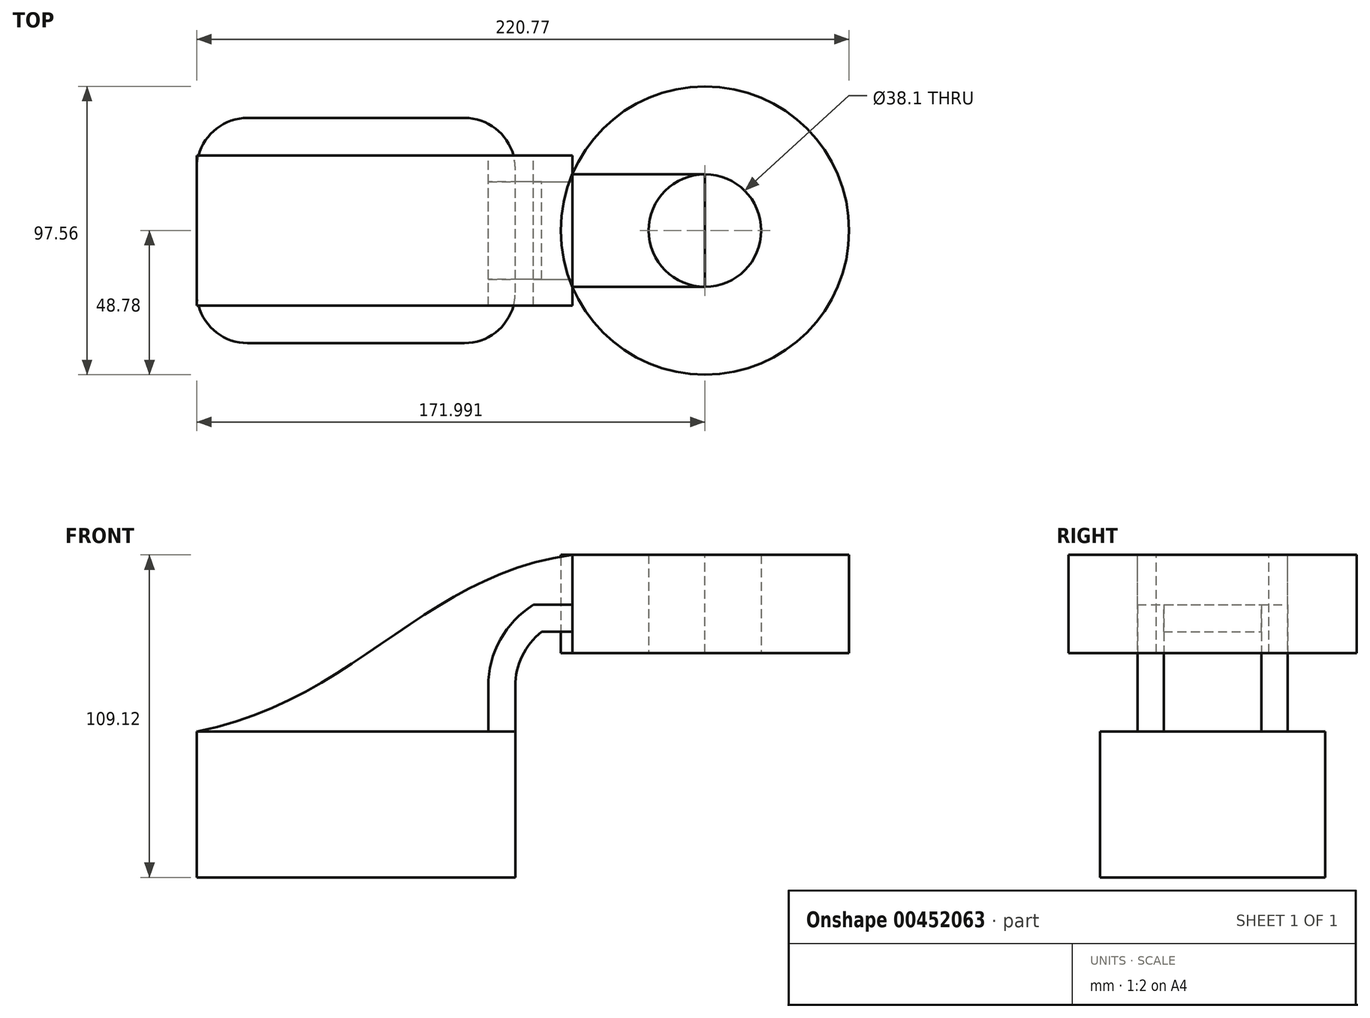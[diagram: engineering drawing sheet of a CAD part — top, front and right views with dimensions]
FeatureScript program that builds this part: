
annotation { "Feature Type Name" : "Feature", "Feature Type Description" : "" }
export const myFeature = defineFeature(function(context is Context, id is Id, definition is map)
    precondition{}
    {
        {
            var Q0;
            Q0=qCreatedBy(makeId("Front.planeOp"),FACE);
            var sketch = newSketch(context, id + "F0", { "sketchPlane" : qUnion([Q0])});
            skLineSegment(sketch, "E0.bottom", {"start": v(-53.89, 24.7) * mm, "end": v(53.89, 24.7) * mm});
            skLineSegment(sketch, "E0.top", {"start": v(-53.89, -24.7) * mm, "end": v(53.89, -24.7) * mm});
            skLineSegment(sketch, "E0.left", {"start": v(-53.89, 24.7) * mm, "end": v(-53.89, -24.7) * mm});
            skLineSegment(sketch, "E0.right", {"start": v(53.89, 24.7) * mm, "end": v(53.89, -24.7) * mm});
            skPoint(sketch, "E0.middle", {"position": v(0, 0) * mm});
            skLineSegment(sketch, "E1.bottom", {"start": v(118.1, 51.2) * mm, "end": v(73.2, 51.2) * mm});
            skLineSegment(sketch, "E1.top", {"start": v(118.1, 84.42) * mm, "end": v(73.2, 84.42) * mm});
            skLineSegment(sketch, "E1.left", {"start": v(118.1, 51.2) * mm, "end": v(118.1, 84.42) * mm});
            skLineSegment(sketch, "E1.right", {"start": v(73.2, 51.2) * mm, "end": v(73.2, 84.42) * mm});
            skPoint(sketch, "E1.middle", {"position": v(95.65, 67.8) * mm});
            skLineSegment(sketch, "E2", {"start": v(53.89, 24.7) * mm, "end": v(53.89, 39.97) * mm});
            skArc(sketch, "E3", {"start": v(62.87, 58.38) * mm, "mid": v(56.25, 50.2) * mm, "end": v(53.89, 39.97) * mm});
            skLineSegment(sketch, "E4", {"start": v(62.87, 58.38) * mm, "end": v(95.65, 58.38) * mm});
            skLineSegment(sketch, "E5.0", {"start": v(60, 67.52) * mm, "end": v(95.65, 67.52) * mm});
            skArc(sketch, "E5.1", {"start": v(60, 67.52) * mm, "mid": v(48.81, 55.72) * mm, "end": v(44.74, 39.97) * mm});
            skLineSegment(sketch, "E5.2", {"start": v(44.74, 24.7) * mm, "end": v(44.74, 39.97) * mm});
            skFitSpline(sketch, "E6", {"points": [v(-53.89, 24.7) * mm, v(73.2, 84.42) * mm], "startDerivative": vector(161.66, 30.98) * mm, "endDerivative": vector(152.23, 20.2) * mm});
            skSolve(sketch);
        }
        {
            var Q0;
            Q0=makeQuery(id+"F0.imprint","IMPRINT",FACE,{"disambiguationData":[TD([[makeQuery(id+"F0.imprint","IMPRINT",EDGE,{"derivedFrom":sQuery(id+"F0.wireOp",EDGE,"E0.top")}),1.0]])]});
            extrude(context, id + "F1", {"entities" : qUnion([Q0]), "endBound" : BoundingType.SYMMETRIC, "depth" : 76.2 * mm});
        }
        {
            var Q0;
            {var subQ1=sQuery(id+"F0.wireOp",EDGE,"E1.bottom");Q0=makeQuery(id+"F0.imprint","IMPRINT",FACE,{"disambiguationData":[TD([[makeQuery(id+"F0.imprint","IMPRINT",EDGE,{"derivedFrom":subQ1}),-1.0]])]});}
            extrude(context, id + "F2", {"entities" : qUnion([Q0]), "endBound" : BoundingType.SYMMETRIC, "depth" : 38.1 * mm});
        }
        {
            var Q0;
            {var subQ0=sQuery(id+"F0.wireOp",EDGE,"E5.1");Q0=makeQuery(id+"F0.imprint","IMPRINT",FACE,{"disambiguationData":[TD([[makeQuery(id+"F0.imprint","IMPRINT",EDGE,{"derivedFrom":subQ0}),-1.0]])]});}
            extrude(context, id + "F3", {"entities" : qUnion([Q0]), "endBound" : BoundingType.SYMMETRIC, "depth" : 50.8 * mm});
        }
        {
            var Q0;
            {var subQ1=sQuery(id+"F0.wireOp",EDGE,"E2");Q0=makeQuery(id+"F0.imprint","IMPRINT",FACE,{"disambiguationData":[TD([[makeQuery(id+"F0.imprint","IMPRINT",EDGE,{"derivedFrom":subQ1}),1.0]])]});}
            extrude(context, id + "F4", {"entities" : qUnion([Q0]), "endBound" : BoundingType.SYMMETRIC, "depth" : 33.02 * mm});
        }
        {
            var Q0;
            Q0=makeQuery(id+"F2.opExtrude","CAP_FACE",FACE,{"disambiguationData":[OSD([sQuery(id+"F0.wireOp",EDGE,"E1.bottom"),sQuery(id+"F0.wireOp",EDGE,"E1.top"),sQuery(id+"F0.wireOp",EDGE,"E1.left"),sQuery(id+"F0.wireOp",EDGE,"E1.right")])],"isStart":false});
            var Q1;
            Q1=sQuery(id+"F0.wireOp",EDGE,"E1.left");
            revolve(context, id + "F5", {"entities" : qUnion([Q0]), "axis" : qUnion([Q1]), "revolveType" : RevolveType.FULL});
        }
        {
            var Q0;
            Q0=makeQuery(id+"F1.opExtrude","CAP_EDGE",EDGE,{"disambiguationData":[OSD([sQuery(id+"F0.wireOp",EDGE,"E0.left")])],"isStart":false});
            var Q1;
            Q1=makeQuery(id+"F1.opExtrude","CAP_EDGE",EDGE,{"disambiguationData":[OSD([sQuery(id+"F0.wireOp",EDGE,"E0.right")])],"isStart":false});
            var Q2;
            Q2=makeQuery(id+"F1.opExtrude","CAP_EDGE",EDGE,{"disambiguationData":[OSD([sQuery(id+"F0.wireOp",EDGE,"E0.right")])],"isStart":true});
            var Q3;
            Q3=makeQuery(id+"F1.opExtrude","CAP_EDGE",EDGE,{"disambiguationData":[OSD([sQuery(id+"F0.wireOp",EDGE,"E0.left")])],"isStart":true});
            fillet(context, id + "F6", {"entities" : qUnion([Q0, Q1, Q2, Q3]), "radius" : 17.17 * mm, "tangentPropagation" : true, "allowEdgeOverflow" : false});
        }
    });
